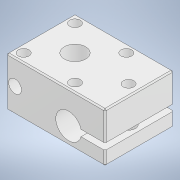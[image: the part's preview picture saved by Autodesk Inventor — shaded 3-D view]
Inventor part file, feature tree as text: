
AUTODESK INVENTOR PART (.ipt)
format: ipt  version: 2022 (Build 260153000, 153)  size: 141,312 bytes
history: imported  units: in
note: dims shown in document units (in); Inventor stores cm internally (conversion verified against a paired STEP export)
features: sketch x2, imported_body x1
ambient origin geometry x8: Origin, YZ Plane, XZ Plane, XY Plane, X Axis, Y Axis, Z Axis, Center Point
bodies: Solid1 (imported_parasolid), Body1 (imported_parasolid)
feature tree (3):
  sketch  "Sketch1"
  sketch  "Sketch2"
  imported_body  NMx_Import_Brep_tag  [imported B-rep: ~44 faces, bbox_mm=[23.0, 11.5, 16.0]]
